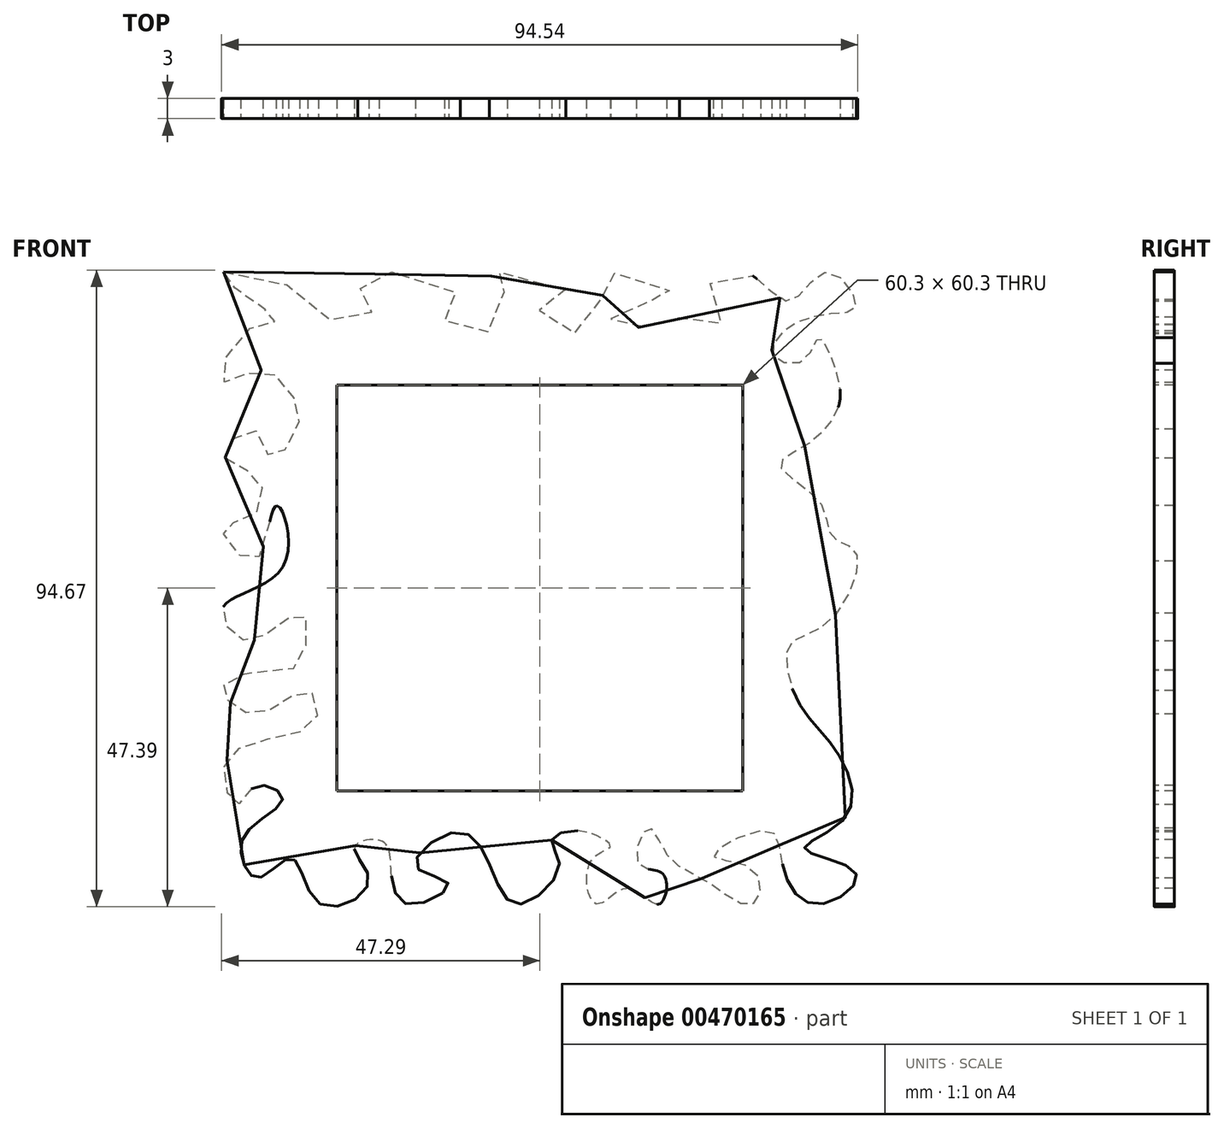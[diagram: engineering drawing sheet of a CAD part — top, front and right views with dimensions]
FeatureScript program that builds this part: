
annotation { "Feature Type Name" : "Feature", "Feature Type Description" : "" }
export const myFeature = defineFeature(function(context is Context, id is Id, definition is map)
    precondition{}
    {
        {
            var Q0;
            Q0=qCreatedBy(makeId("Front.planeOp"),FACE);
            var sketch = newSketch(context, id + "F0", { "sketchPlane" : qUnion([Q0])});
            skLineSegment(sketch, "E0.bottom", {"start": v(-28.65, 28.65) * mm, "end": v(28.65, 28.65) * mm});
            skLineSegment(sketch, "E0.top", {"start": v(-28.65, -28.65) * mm, "end": v(28.65, -28.65) * mm});
            skLineSegment(sketch, "E0.left", {"start": v(-28.65, 28.65) * mm, "end": v(-28.65, -28.65) * mm});
            skLineSegment(sketch, "E0.right", {"start": v(28.65, 28.65) * mm, "end": v(28.65, -28.65) * mm});
            skLineSegment(sketch, "E1", {"start": v(28.65, 28.65) * mm, "end": v(-28.65, -28.65) * mm, "construction": true});
            skLineSegment(sketch, "E2.bottom", {"start": v(18.16, 26.65) * mm, "end": v(-18.16, 26.65) * mm});
            skLineSegment(sketch, "E2.top", {"start": v(18.16, -26.65) * mm, "end": v(-18.16, -26.65) * mm});
            skLineSegment(sketch, "E2.left", {"start": v(26.65, 18.16) * mm, "end": v(26.65, -18.16) * mm});
            skLineSegment(sketch, "E2.right", {"start": v(-26.65, 18.16) * mm, "end": v(-26.65, -18.16) * mm});
            skLineSegment(sketch, "E3", {"start": v(18.16, 26.65) * mm, "end": v(26.65, 18.16) * mm});
            skPoint(sketch, "E4.orphan", {"position": v(26.65, 26.65) * mm});
            skLineSegment(sketch, "E5.1.0", {"start": v(-26.65, 18.16) * mm, "end": v(-18.16, 26.65) * mm});
            skLineSegment(sketch, "E5.2.0", {"start": v(-18.16, -26.65) * mm, "end": v(-26.65, -18.16) * mm});
            skLineSegment(sketch, "E5.3.0", {"start": v(26.65, -18.16) * mm, "end": v(18.16, -26.65) * mm});
            skPoint(sketch, "E5.center", {"position": v(0, 0) * mm});
            skSolve(sketch);
        }
        {
            var Q0;
            Q0 = qSketchRegion(id + "F0", true);
            extrude(context, id + "F1", {"entities" : qUnion([Q0]), "depth" : 1.5 * mm});
        }
        {
            var Q0;
            Q0=qCreatedBy(makeId("Front.planeOp"),FACE);
            var sketch = newSketch(context, id + "F2", { "sketchPlane" : qUnion([Q0])});
            skLineSegment(sketch, "E6.0", {"start": v(-28.65, 30.15) * mm, "end": v(28.65, 30.15) * mm});
            skLineSegment(sketch, "E7.0", {"start": v(30.15, 28.65) * mm, "end": v(30.15, -28.65) * mm});
            skLineSegment(sketch, "E8.0", {"start": v(-28.65, -30.15) * mm, "end": v(28.65, -30.15) * mm});
            skLineSegment(sketch, "E9.0", {"start": v(-30.15, 28.65) * mm, "end": v(-30.15, -28.65) * mm});
            skLineSegment(sketch, "E10", {"start": v(-28.65, 30.15) * mm, "end": v(-30.15, 30.15) * mm});
            skLineSegment(sketch, "E11", {"start": v(-30.15, 30.15) * mm, "end": v(-30.15, 28.65) * mm});
            skLineSegment(sketch, "E12", {"start": v(-30.15, -28.65) * mm, "end": v(-30.15, -30.15) * mm});
            skLineSegment(sketch, "E13", {"start": v(-30.15, -30.15) * mm, "end": v(-28.65, -30.15) * mm});
            skLineSegment(sketch, "E14", {"start": v(30.15, -28.65) * mm, "end": v(30.15, -30.15) * mm});
            skLineSegment(sketch, "E15", {"start": v(30.15, -30.15) * mm, "end": v(28.65, -30.15) * mm});
            skLineSegment(sketch, "E16", {"start": v(28.65, 30.15) * mm, "end": v(30.15, 30.15) * mm});
            skPoint(sketch, "E16.endSnap0", {"position": v(30.15, 0) * mm});
            skLineSegment(sketch, "E17", {"start": v(30.15, 30.15) * mm, "end": v(30.15, 28.65) * mm});
            skLineSegment(sketch, "E18.0", {"start": v(-28.65, 28.65) * mm, "end": v(28.65, 28.65) * mm});
            skLineSegment(sketch, "E19.0", {"start": v(-28.65, 28.65) * mm, "end": v(-28.65, -28.65) * mm});
            skLineSegment(sketch, "E20.0", {"start": v(-28.65, -28.65) * mm, "end": v(28.65, -28.65) * mm});
            skLineSegment(sketch, "E21.0", {"start": v(28.65, 28.65) * mm, "end": v(28.65, -28.65) * mm});
            skSolve(sketch);
        }
        {
            var Q0;
            Q0 = qSketchRegion(id + "F2", true);
            extrude(context, id + "F3", {"entities" : qUnion([Q0]), "operationType" : NewBodyOperationType.ADD, "depth" : 7 * mm});
        }
        {
            var Q0;
            Q0=qCreatedBy(makeId("Front.planeOp"),FACE);
            var sketch = newSketch(context, id + "F4", { "sketchPlane" : qUnion([Q0])});
            skLineSegment(sketch, "E22", {"start": v(25.58, 0) * mm, "end": v(25.58, 6) * mm});
            skLineSegment(sketch, "E23", {"start": v(25.58, 6) * mm, "end": v(33.95, 6) * mm});
            skLineSegment(sketch, "E24", {"start": v(33.95, 6) * mm, "end": v(33.95, -6) * mm});
            skLineSegment(sketch, "E25", {"start": v(33.95, -6) * mm, "end": v(25.58, -6) * mm});
            skLineSegment(sketch, "E26", {"start": v(25.58, -6) * mm, "end": v(25.58, 0) * mm});
            skLineSegment(sketch, "E27.1.0", {"start": v(-6, 25.58) * mm, "end": v(-6, 33.95) * mm});
            skLineSegment(sketch, "E27.1.1", {"start": v(-6, 33.95) * mm, "end": v(6, 33.95) * mm});
            skLineSegment(sketch, "E27.1.2", {"start": v(6, 25.58) * mm, "end": v(0, 25.58) * mm});
            skLineSegment(sketch, "E27.1.3", {"start": v(0, 25.58) * mm, "end": v(-6, 25.58) * mm});
            skLineSegment(sketch, "E27.1.4", {"start": v(6, 33.95) * mm, "end": v(6, 25.58) * mm});
            skLineSegment(sketch, "E27.2.0", {"start": v(-25.58, -6) * mm, "end": v(-33.95, -6) * mm});
            skLineSegment(sketch, "E27.2.1", {"start": v(-33.95, -6) * mm, "end": v(-33.95, 6) * mm});
            skLineSegment(sketch, "E27.2.2", {"start": v(-25.58, 6) * mm, "end": v(-25.58, 0) * mm});
            skLineSegment(sketch, "E27.2.3", {"start": v(-25.58, 0) * mm, "end": v(-25.58, -6) * mm});
            skLineSegment(sketch, "E27.2.4", {"start": v(-33.95, 6) * mm, "end": v(-25.58, 6) * mm});
            skLineSegment(sketch, "E27.3.0", {"start": v(6, -25.58) * mm, "end": v(6, -33.95) * mm});
            skLineSegment(sketch, "E27.3.1", {"start": v(6, -33.95) * mm, "end": v(-6, -33.95) * mm});
            skLineSegment(sketch, "E27.3.2", {"start": v(-6, -25.58) * mm, "end": v(0, -25.58) * mm});
            skLineSegment(sketch, "E27.3.3", {"start": v(0, -25.58) * mm, "end": v(6, -25.58) * mm});
            skLineSegment(sketch, "E27.3.4", {"start": v(-6, -33.95) * mm, "end": v(-6, -25.58) * mm});
            skPoint(sketch, "E27.center", {"position": v(0, 0) * mm});
            skSolve(sketch);
        }
        {
            var Q0;
            Q0=makeQuery(id+"F4.imprint","IMPRINT",FACE,{"disambiguationData":[TD([[makeQuery(id+"F4.imprint","IMPRINT",EDGE,{"derivedFrom":sQuery(id+"F4.wireOp",EDGE,"E22")}),-1.0]])]});
            var Q1;
            Q1=makeQuery(id+"F4.imprint","IMPRINT",FACE,{"disambiguationData":[TD([[makeQuery(id+"F4.imprint","IMPRINT",EDGE,{"derivedFrom":sQuery(id+"F4.wireOp",EDGE,"E27.1.0")}),-1.0]])]});
            var Q2;
            Q2=makeQuery(id+"F4.imprint","IMPRINT",FACE,{"disambiguationData":[TD([[makeQuery(id+"F4.imprint","IMPRINT",EDGE,{"derivedFrom":sQuery(id+"F4.wireOp",EDGE,"E27.2.0")}),-1.0]])]});
            var Q3;
            Q3=makeQuery(id+"F4.imprint","IMPRINT",FACE,{"disambiguationData":[TD([[makeQuery(id+"F4.imprint","IMPRINT",EDGE,{"derivedFrom":sQuery(id+"F4.wireOp",EDGE,"E27.3.0")}),-1.0]])]});
            extrude(context, id + "F5", {"entities" : qUnion([Q0, Q1, Q2, Q3]), "operationType" : NewBodyOperationType.REMOVE, "depth" : 2.5 * mm});
        }
        {
            var Q0;
            Q0=makeQuery(id+"F3.opExtrude","CAP_FACE",FACE,{"disambiguationData":[OSD([sQuery(id+"F2.wireOp",EDGE,"E6.0"),sQuery(id+"F2.wireOp",EDGE,"E7.0"),sQuery(id+"F2.wireOp",EDGE,"E8.0"),sQuery(id+"F2.wireOp",EDGE,"E9.0"),sQuery(id+"F2.wireOp",EDGE,"E10"),sQuery(id+"F2.wireOp",EDGE,"E11"),sQuery(id+"F2.wireOp",EDGE,"E12"),sQuery(id+"F2.wireOp",EDGE,"E13"),sQuery(id+"F2.wireOp",EDGE,"E14"),sQuery(id+"F2.wireOp",EDGE,"E15"),sQuery(id+"F2.wireOp",EDGE,"E16"),sQuery(id+"F2.wireOp",EDGE,"E17"),sQuery(id+"F2.wireOp",EDGE,"E18.0"),sQuery(id+"F2.wireOp",EDGE,"E19.0"),sQuery(id+"F2.wireOp",EDGE,"E20.0"),sQuery(id+"F2.wireOp",EDGE,"E21.0")])],"isStart":false});
            var sketch = newSketch(context, id + "F6", { "sketchPlane" : qUnion([Q0])});
            skPoint(sketch, "E28.center", {"position": v(0, 0) * mm});
            skLineSegment(sketch, "E29.0", {"start": v(-30.15, 30.15) * mm, "end": v(-30.15, 28.65) * mm});
            skLineSegment(sketch, "E29.1", {"start": v(30.15, -30.15) * mm, "end": v(28.65, -30.15) * mm});
            skLineSegment(sketch, "E29.2", {"start": v(-28.65, -30.15) * mm, "end": v(28.65, -30.15) * mm});
            skLineSegment(sketch, "E29.3", {"start": v(-30.15, -30.15) * mm, "end": v(-28.65, -30.15) * mm});
            skLineSegment(sketch, "E29.4", {"start": v(-30.15, -28.65) * mm, "end": v(-30.15, -30.15) * mm});
            skLineSegment(sketch, "E29.5", {"start": v(30.15, -28.65) * mm, "end": v(30.15, -30.15) * mm});
            skLineSegment(sketch, "E29.6", {"start": v(-30.15, 28.65) * mm, "end": v(-30.15, -28.65) * mm});
            skLineSegment(sketch, "E29.7", {"start": v(30.15, 28.65) * mm, "end": v(30.15, -28.65) * mm});
            skLineSegment(sketch, "E29.8", {"start": v(30.15, 30.15) * mm, "end": v(30.15, 28.65) * mm});
            skLineSegment(sketch, "E29.9", {"start": v(28.65, 30.15) * mm, "end": v(30.15, 30.15) * mm});
            skLineSegment(sketch, "E29.10", {"start": v(-28.65, 30.15) * mm, "end": v(28.65, 30.15) * mm});
            skLineSegment(sketch, "E29.11", {"start": v(-28.65, 30.15) * mm, "end": v(-30.15, 30.15) * mm});
            skPoint(sketch, "E30.73.internal.snap0", {"position": v(-23.5, 47) * mm});
            skPoint(sketch, "E30.106.internal.snap0", {"position": v(-47, 23.5) * mm});
            skPoint(sketch, "E30.108.internal.snap0", {"position": v(-47, 23.5) * mm});
            skFitSpline(sketch, "E30", {"points": [v(-47, 47) * mm, v(-32.97, 42.48) * mm, v(-30.06, 39.18) * mm, v(-23.86, 42.48) * mm, v(-26.96, 44.8) * mm, v(-21.72, 47) * mm, v(-11.83, 42.48) * mm, v(-14.16, 39.57) * mm, v(-6.79, 38.4) * mm, v(-5.63, 44.61) * mm, v(-7.37, 47) * mm, v(3.88, 44.03) * mm, v(0, 41.7) * mm, v(4.27, 37.82) * mm, v(7.95, 40.93) * mm, v(10.09, 45.2) * mm, v(12.03, 47) * mm, v(20.75, 42.87) * mm, v(11.64, 42.28) * mm, v(11.25, 38.6) * mm, v(16.3, 39.37) * mm, v(20.95, 40.15) * mm, v(26.96, 39.37) * mm, v(25.22, 44.8) * mm, v(30.45, 47) * mm, v(37.24, 42.67) * mm, v(42.67, 47) * mm, v(47, 41.9) * mm, v(43.06, 40.73) * mm, v(36.27, 38.21) * mm, v(34.72, 34.53) * mm, v(39.37, 33.94) * mm, v(41.5, 37.24) * mm, v(44.22, 31.42) * mm, v(44.22, 26.57) * mm, v(39.76, 21.34) * mm, v(35.69, 18.23) * mm, v(41.7, 12.6) * mm, v(43.45, 7.56) * mm, v(47, 5.24) * mm, v(42.48, -5.43) * mm, v(37.05, -8.53) * mm, v(38.6, -17.26) * mm, v(44.22, -24.44) * mm, v(45.39, -34.14) * mm, v(39.37, -38.8) * mm, v(47, -42.48) * mm, v(41.12, -47) * mm, v(36.08, -41.12) * mm, v(33.94, -36.08) * mm, v(25.8, -39.76) * mm, v(31.81, -41.9) * mm, v(31.62, -47) * mm, v(24.83, -43.64) * mm, v(19, -39.76) * mm, v(16.1, -35.69) * mm, v(14.55, -40.93) * mm, v(18.43, -42.67) * mm, v(17.65, -47) * mm, v(13, -44.61) * mm, v(8.34, -47) * mm, v(7.56, -40.54) * mm, v(10.47, -38.4) * mm, v(5.82, -36.08) * mm, v(1.75, -37.63) * mm, v(2.9, -41.31) * mm, v(-3.3, -47) * mm, v(-7.37, -41.31) * mm, v(-12.41, -36.27) * mm, v(-18.43, -41.31) * mm, v(-13.58, -44.03) * mm, v(-19.6, -47) * mm, v(-22.11, -41.9) * mm, v(-23.5, -37.63) * mm, v(-27.54, -38.6) * mm, v(-25.4, -43.64) * mm, v(-32.59, -47) * mm, v(-36.85, -40.15) * mm, v(-41.7, -43.06) * mm, v(-44.22, -40.34) * mm, v(-43.06, -35.69) * mm, v(-38.21, -31.23) * mm, v(-42.28, -29.48) * mm, v(-45, -32.2) * mm, v(-47, -27.35) * mm, v(-42.48, -22.89) * mm, v(-33.36, -19.78) * mm, v(-34.33, -15.32) * mm, v(-40.73, -18.43) * mm, v(-45.58, -17.46) * mm, v(-47, -14.55) * mm, v(-40.54, -12.22) * mm, v(-35.88, -11.25) * mm, v(-35.1, -3.88) * mm, v(-41.5, -7.37) * mm, v(-45.39, -6.98) * mm, v(-47, -2.72) * mm, v(-38.02, 3.5) * mm, v(-39.18, 12.22) * mm, v(-41.9, 4.46) * mm, v(-45.2, 5.43) * mm, v(-47, 9.12) * mm, v(-42.87, 10.47) * mm, v(-41.31, 15.13) * mm, v(-44.61, 18.04) * mm, v(-47, 20.37) * mm, v(-42.48, 23.5) * mm, v(-39.96, 19.4) * mm, v(-36.08, 23.5) * mm, v(-36.66, 28.51) * mm, v(-41.7, 32.4) * mm, v(-47, 30.65) * mm, v(-44.03, 38.02) * mm, v(-39.18, 39.76) * mm, v(-43.84, 43.45) * mm, v(-47, 47) * mm]});
            skPoint(sketch, "E31.orphan", {"position": v(0, 47) * mm});
            skPoint(sketch, "E28.1.1.start.orphan", {"position": v(-47, 0) * mm});
            skSolve(sketch);
        }
        {
            var Q0;
            Q0=makeQuery(id+"F6.imprint","IMPRINT",FACE,{"disambiguationData":[TD([[makeQuery(id+"F6.imprint","IMPRINT",EDGE,{"derivedFrom":sQuery(id+"F6.wireOp",EDGE,"E29.0")}),-1.0]])]});
            extrude(context, id + "F7", {"entities" : qUnion([Q0]), "operationType" : NewBodyOperationType.ADD, "oppositeDirection" : true, "depth" : 3 * mm});
        }
        {
            var Q0;
            Q0=makeQuery(id+"F7.boolean.opBoolean","MERGE",FACE,{"derivedFrom":[makeQuery(id+"F3.opExtrude","CAP_FACE",FACE,{"disambiguationData":[OSD([sQuery(id+"F2.wireOp",EDGE,"E6.0"),sQuery(id+"F2.wireOp",EDGE,"E7.0"),sQuery(id+"F2.wireOp",EDGE,"E8.0"),sQuery(id+"F2.wireOp",EDGE,"E9.0"),sQuery(id+"F2.wireOp",EDGE,"E10"),sQuery(id+"F2.wireOp",EDGE,"E11"),sQuery(id+"F2.wireOp",EDGE,"E12"),sQuery(id+"F2.wireOp",EDGE,"E13"),sQuery(id+"F2.wireOp",EDGE,"E14"),sQuery(id+"F2.wireOp",EDGE,"E15"),sQuery(id+"F2.wireOp",EDGE,"E16"),sQuery(id+"F2.wireOp",EDGE,"E17"),sQuery(id+"F2.wireOp",EDGE,"E18.0"),sQuery(id+"F2.wireOp",EDGE,"E19.0"),sQuery(id+"F2.wireOp",EDGE,"E20.0"),sQuery(id+"F2.wireOp",EDGE,"E21.0")])],"isStart":false}),makeQuery(id+"F7.opExtrude","CAP_FACE",FACE,{"disambiguationData":[OSD([sQuery(id+"F6.wireOp",EDGE,"E29.0"),sQuery(id+"F6.wireOp",EDGE,"E29.1"),sQuery(id+"F6.wireOp",EDGE,"E29.2"),sQuery(id+"F6.wireOp",EDGE,"E29.3"),sQuery(id+"F6.wireOp",EDGE,"E29.4"),sQuery(id+"F6.wireOp",EDGE,"E29.5"),sQuery(id+"F6.wireOp",EDGE,"E29.6"),sQuery(id+"F6.wireOp",EDGE,"E29.7"),sQuery(id+"F6.wireOp",EDGE,"E29.8"),sQuery(id+"F6.wireOp",EDGE,"E29.9"),sQuery(id+"F6.wireOp",EDGE,"E29.10"),sQuery(id+"F6.wireOp",EDGE,"E29.11"),sQuery(id+"F6.wireOp",EDGE,"E30")])],"isStart":true})]});
            var sketch = newSketch(context, id + "F8", { "sketchPlane" : qUnion([Q0])});
            skLineSegment(sketch, "E32.0", {"start": v(-30.15, 30.15) * mm, "end": v(30.15, 30.15) * mm});
            skLineSegment(sketch, "E32.1", {"start": v(-30.15, 30.15) * mm, "end": v(-30.15, -30.15) * mm});
            skLineSegment(sketch, "E32.2", {"start": v(-30.15, -30.15) * mm, "end": v(30.15, -30.15) * mm});
            skLineSegment(sketch, "E32.3", {"start": v(30.15, 30.15) * mm, "end": v(30.15, -30.15) * mm});
            skSolve(sketch);
        }
        {
            var Q0;
            Q0 = qSketchRegion(id + "F8", true);
            extrude(context, id + "F9", {"entities" : qUnion([Q0]), "operationType" : NewBodyOperationType.REMOVE, "oppositeDirection" : true, "depth" : 25 * mm});
        }
    });
